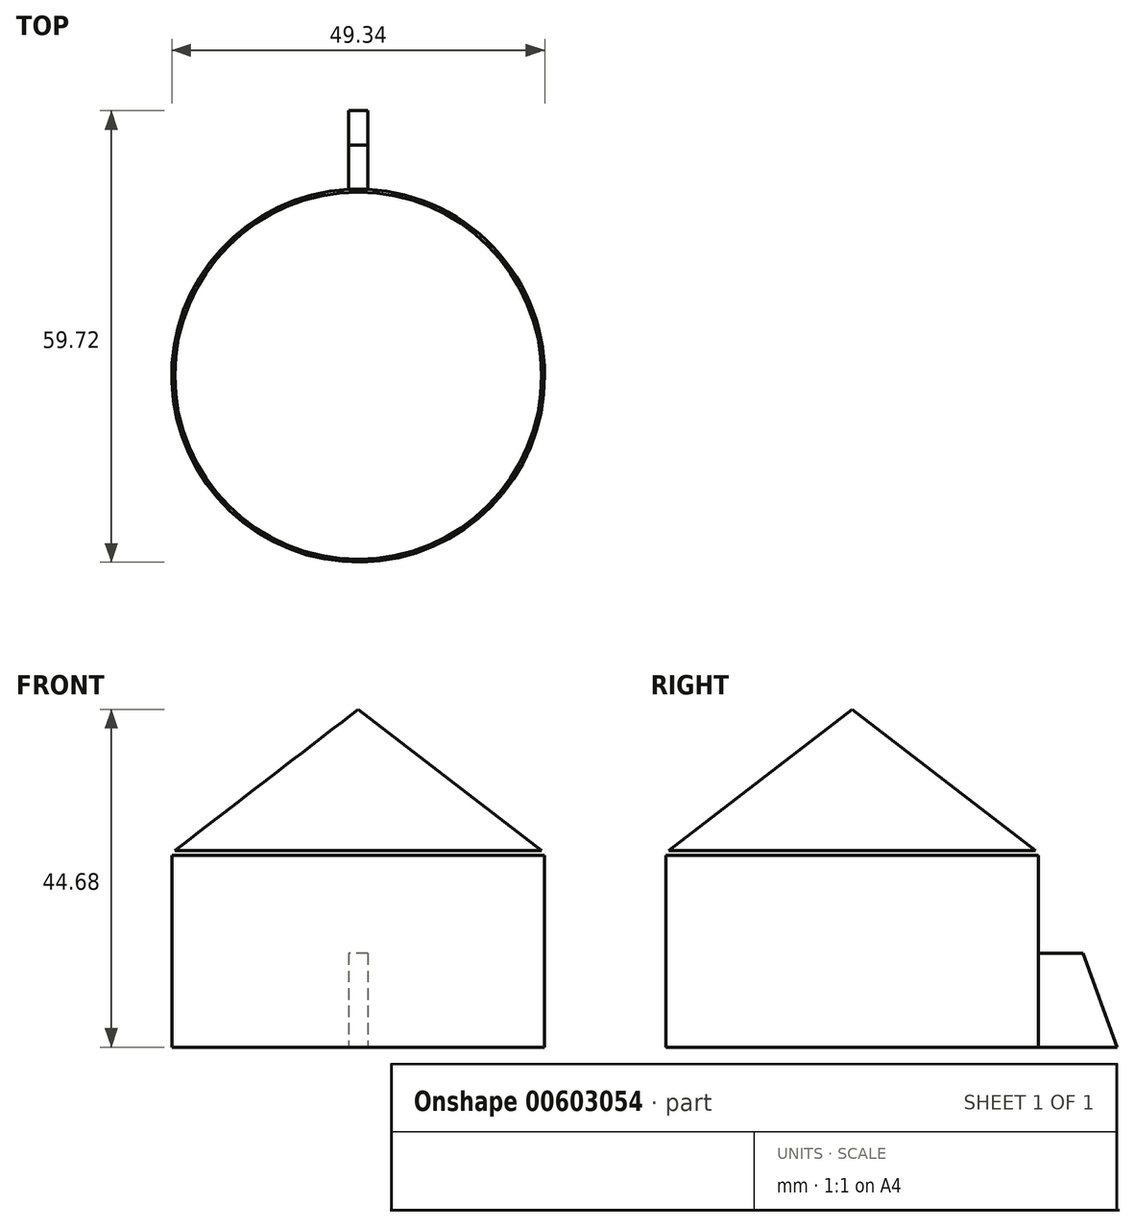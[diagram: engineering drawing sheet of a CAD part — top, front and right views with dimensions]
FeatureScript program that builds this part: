
annotation { "Feature Type Name" : "Feature", "Feature Type Description" : "" }
export const myFeature = defineFeature(function(context is Context, id is Id, definition is map)
    precondition{}
    {
        {
            var Q0;
            Q0=qCreatedBy(makeId("Top.planeOp"),FACE);
            var sketch = newSketch(context, id + "F0", { "sketchPlane" : qUnion([Q0])});
            skCircle(sketch, "E0", {"center": v(0, 0) * mm, "radius": 24.67 * mm});
            skSolve(sketch);
        }
        {
            var Q0;
            Q0=makeQuery(id+"F0.imprint","IMPRINT",FACE,{"disambiguationData":[TD([[makeQuery(id+"F0.imprint","IMPRINT",EDGE,{"derivedFrom":sQuery(id+"F0.wireOp",EDGE,"E0")}),1.0]])]});
            extrude(context, id + "F1", {"entities" : qUnion([Q0]), "depth" : 25.4 * mm, "offsetDistance" : 25.4 * mm});
        }
        {
            var Q0;
            Q0=qCreatedBy(makeId("Right.planeOp"),FACE);
            var sketch = newSketch(context, id + "F2", { "sketchPlane" : qUnion([Q0])});
            skLineSegment(sketch, "E1", {"start": v(0, 44.68) * mm, "end": v(24.29, 25.99) * mm});
            skLineSegment(sketch, "E2", {"start": v(0, 44.68) * mm, "end": v(0, 25.99) * mm});
            skLineSegment(sketch, "E3", {"start": v(0, 25.99) * mm, "end": v(24.29, 25.99) * mm});
            skSolve(sketch);
        }
        {
            var Q0;
            Q0=makeQuery(id+"F2.imprint","IMPRINT",FACE,{"disambiguationData":[TD([[makeQuery(id+"F2.imprint","IMPRINT",EDGE,{"derivedFrom":sQuery(id+"F2.wireOp",EDGE,"E1")}),-1.0]])]});
            var Q1;
            Q1=sQuery(id+"F2.wireOp",EDGE,"E2");
            revolve(context, id + "F3", {"entities" : qUnion([Q0]), "axis" : qUnion([Q1]), "revolveType" : RevolveType.FULL});
        }
        {
            var Q0;
            Q0=qCreatedBy(makeId("Right.planeOp"),FACE);
            var sketch = newSketch(context, id + "F4", { "sketchPlane" : qUnion([Q0])});
            skLineSegment(sketch, "E4", {"start": v(0, 12.4) * mm, "end": v(30.52, 12.4) * mm});
            skLineSegment(sketch, "E5", {"start": v(30.52, 12.4) * mm, "end": v(35.05, 0) * mm});
            skLineSegment(sketch, "E6", {"start": v(35.05, 0) * mm, "end": v(0, 0) * mm});
            skLineSegment(sketch, "E7", {"start": v(0, 0) * mm, "end": v(0, 12.4) * mm});
            skSolve(sketch);
        }
        {
            var Q0;
            Q0=makeQuery(id+"F4.imprint","IMPRINT",FACE,{"disambiguationData":[TD([[makeQuery(id+"F4.imprint","IMPRINT",EDGE,{"derivedFrom":sQuery(id+"F4.wireOp",EDGE,"E4")}),-1.0]])]});
            extrude(context, id + "F5", {"entities" : qUnion([Q0]), "operationType" : NewBodyOperationType.ADD, "depth" : 1.27 * mm, "offsetDistance" : 25.4 * mm, "hasSecondDirection" : true, "secondDirectionOppositeDirection" : true, "secondDirectionDepth" : 1.27 * mm});
        }
    });
